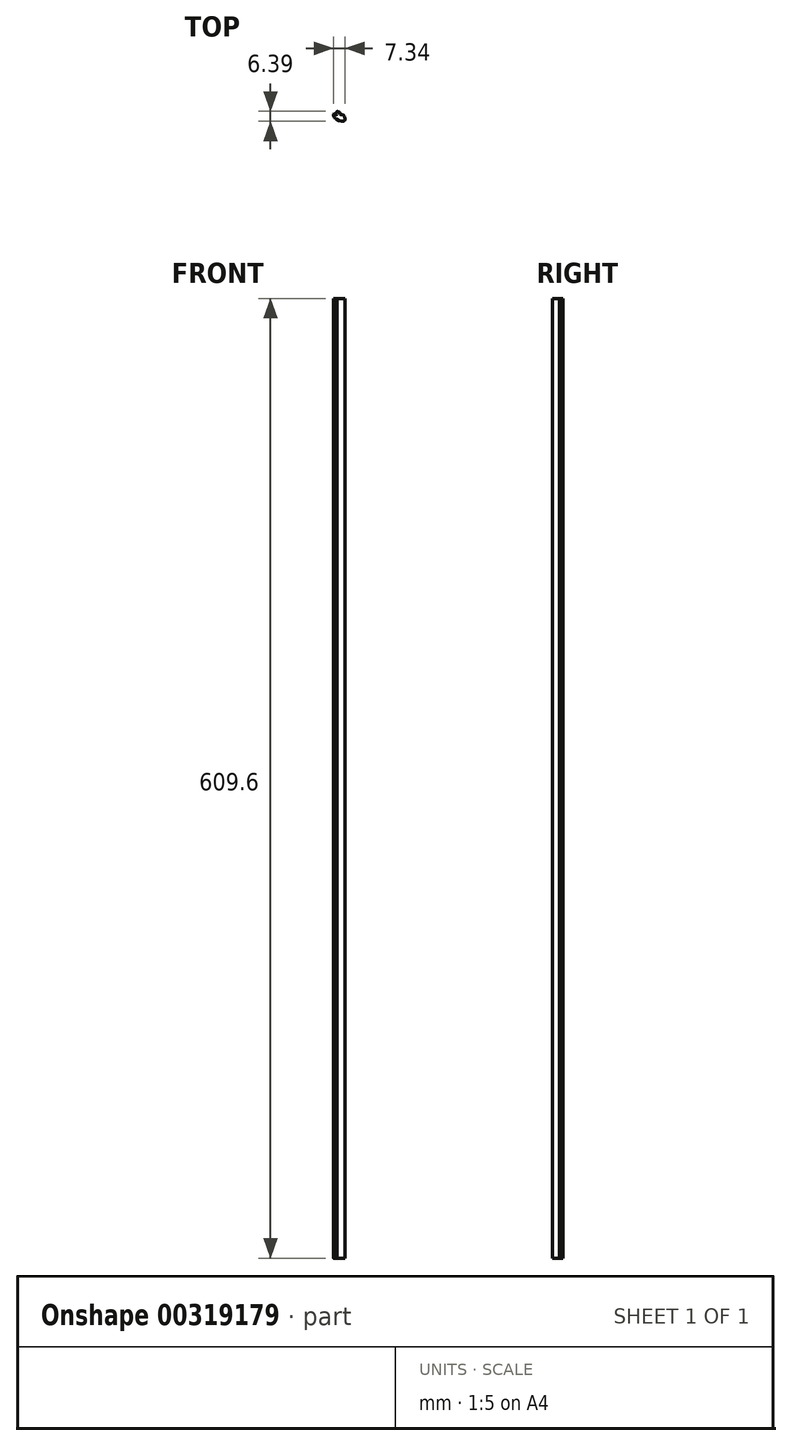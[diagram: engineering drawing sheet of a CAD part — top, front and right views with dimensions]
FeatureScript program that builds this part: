
annotation { "Feature Type Name" : "Feature", "Feature Type Description" : "" }
export const myFeature = defineFeature(function(context is Context, id is Id, definition is map)
    precondition{}
    {
        {
            var Q0;
            Q0=qCreatedBy(makeId("Top.planeOp"),FACE);
            var sketch = newSketch(context, id + "F0", { "sketchPlane" : qUnion([Q0])});
            skFitSpline(sketch, "E0", {"points": [v(-54.66, -21.02) * mm, v(-55.03, -18.48) * mm, v(-53.2, -19.16) * mm, v(-53.3, -17.2) * mm, v(-51.49, -17.6) * mm, v(-51.08, -18.8) * mm, v(-49.13, -19.42) * mm, v(-48.51, -22.98) * mm, v(-54.66, -21.02) * mm]});
            skFitSpline(sketch, "E1.MirrorC", {"points": [v(-54.66, 12.8) * mm, v(-55.03, 10.25) * mm, v(-53.2, 10.93) * mm, v(-53.3, 8.97) * mm, v(-51.49, 9.37) * mm, v(-51.08, 10.58) * mm, v(-49.13, 11.2) * mm, v(-48.51, 14.75) * mm, v(-54.66, 12.8) * mm]});
            skSolve(sketch);
        }
        {
            var Q0;
            Q0=makeQuery(id+"F0.imprint","IMPRINT",FACE,{"disambiguationData":[TD([[makeQuery(id+"F0.imprint","IMPRINT",EDGE,{"derivedFrom":sQuery(id+"F0.wireOp",EDGE,"E0")}),-1.0]])]});
            extrude(context, id + "F1", {"entities" : qUnion([Q0]), "depth" : 609.6 * mm});
        }
    });
